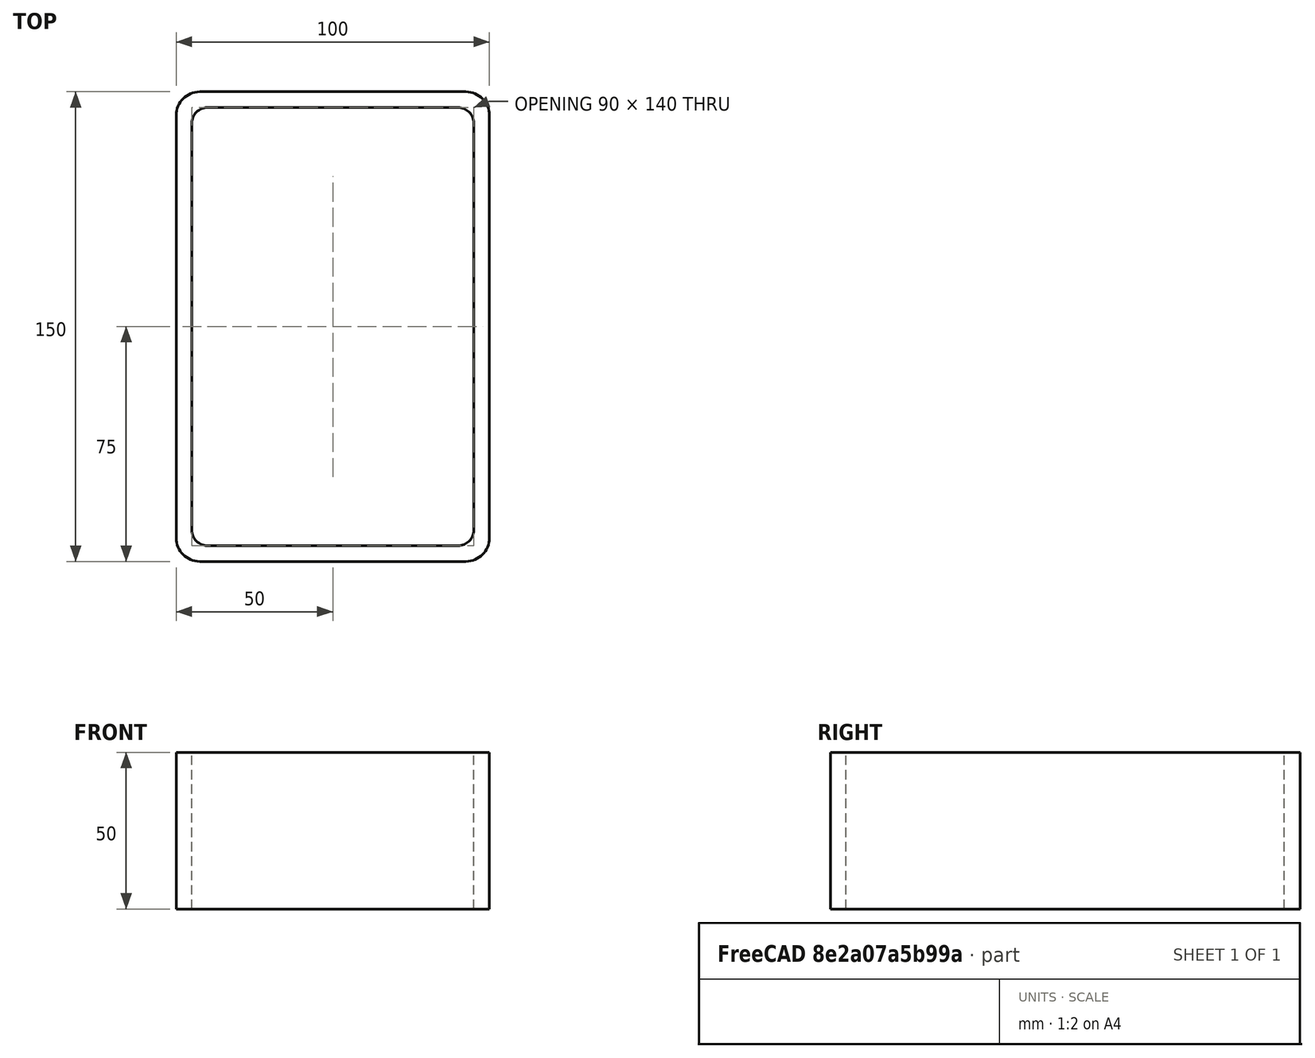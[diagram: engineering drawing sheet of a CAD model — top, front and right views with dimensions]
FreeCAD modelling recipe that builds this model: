
FCSTD DOCUMENT  (FreeCAD 0.15R4671 (Git))
Label: Rectangular hollow section 150x100x5 EN10219 S235JRH
License: All rights reserved
LicenseURL: http://en.wikipedia.org/wiki/All_rights_reserved
objects: Sketcher::SketchObject×1, Part::Extrusion×1
note: 2 computed .brp shape members not serialized (recipe doc carries the construction recipe); baked Part::Feature solids carry a one-line shape summary decoded from their .brp

FEATURE [Sketcher::SketchObject] Sketch
  sketch-geometry (16):
    g0: LineSegment StartX=-40 StartY=70 StartZ=0 EndX=40 EndY=70 EndZ=0
    g1: LineSegment StartX=45 StartY=65 StartZ=0 EndX=45 EndY=-65 EndZ=0
    g2: LineSegment StartX=40 StartY=-70 StartZ=0 EndX=-40 EndY=-70 EndZ=0
    g3: LineSegment StartX=-45 StartY=-65 StartZ=0 EndX=-45 EndY=65 EndZ=0
    g4: LineSegment StartX=-42.5 StartY=75 StartZ=0 EndX=42.5 EndY=75 EndZ=0
    g5: LineSegment StartX=50 StartY=67.5 StartZ=0 EndX=50 EndY=-67.5 EndZ=0
    g6: LineSegment StartX=42.5 StartY=-75 StartZ=0 EndX=-42.5 EndY=-75 EndZ=0
    g7: LineSegment StartX=-50 StartY=-67.5 StartZ=0 EndX=-50 EndY=67.5 EndZ=0
    g8: ArcOfCircle CenterX=-40 CenterY=65 CenterZ=0 NormalX=0 NormalY=0 NormalZ=1 Radius=5 StartAngle=1.5708 EndAngle=3.14159
    g9: ArcOfCircle CenterX=40 CenterY=65 CenterZ=0 NormalX=0 NormalY=0 NormalZ=1 Radius=5 StartAngle=0 EndAngle=1.5708
    g10: ArcOfCircle CenterX=40 CenterY=-65 CenterZ=0 NormalX=0 NormalY=0 NormalZ=1 Radius=5 StartAngle=4.71239 EndAngle=6.28319
    g11: ArcOfCircle CenterX=-40 CenterY=-65 CenterZ=0 NormalX=0 NormalY=0 NormalZ=1 Radius=5 StartAngle=3.14159 EndAngle=4.71239
    g12: ArcOfCircle CenterX=42.5 CenterY=67.5 CenterZ=0 NormalX=0 NormalY=0 NormalZ=1 Radius=7.5 StartAngle=0 EndAngle=1.5708
    g13: ArcOfCircle CenterX=42.5 CenterY=-67.5 CenterZ=0 NormalX=0 NormalY=0 NormalZ=1 Radius=7.5 StartAngle=4.71239 EndAngle=6.28319
    g14: ArcOfCircle CenterX=-42.5 CenterY=-67.5 CenterZ=0 NormalX=0 NormalY=0 NormalZ=1 Radius=7.5 StartAngle=3.14159 EndAngle=4.71239
    g15: ArcOfCircle CenterX=-42.5 CenterY=67.5 CenterZ=0 NormalX=0 NormalY=0 NormalZ=1 Radius=7.5 StartAngle=1.5708 EndAngle=3.14159
  constraints (36):
    c: Horizontal(g2)
    c: Vertical(g3)
    c: Horizontal(g6)
    c: Vertical(g7)
    c: Tangent(g3,g8) = 1.5708
    c: Tangent(g0,g8) = 1.5708
    c: Tangent(g0,g9) = 1.5708
    c: Tangent(g1,g9) = 1.5708
    c: Tangent(g1,g10) = 1.5708
    c: Tangent(g2,g10) = 1.5708
    c: Tangent(g2,g11) = 1.5708
    c: Tangent(g3,g11) = 1.5708
    c: Tangent(g4,g12) = 1.5708
    c: Tangent(g5,g12) = 1.5708
    c: Tangent(g5,g13) = 1.5708
    c: Tangent(g6,g13) = 1.5708
    c: Tangent(g6,g14) = 1.5708
    c: Tangent(g7,g14) = 1.5708
    c: Tangent(g7,g15) = 1.5708
    c: Tangent(g4,g15) = 1.5708
    c: Equal(g9,g8)
    c: Equal(g9,g11)
    c: Equal(g9,g10)
    c: Equal(g12,g15)
    c: Equal(g12,g14)
    c: Equal(g12,g13)
    c: Symmetric(g4,g6,g-1)
    c: Symmetric(g7,g5,g-2)
    c: DistanceY(g4,g6) = -150
    c: DistanceX(g7,g5) = 100
    c: Symmetric(g3,g1,g-2)
    c: Symmetric(g0,g2,g-1)
    c: DistanceY(g0,g4) = 5
    c: DistanceX(g5,g1) = -5
    c: Radius(g9) = 5
    c: Radius(g12) = 7.5
FEATURE [Part::Extrusion] Extrude  label="Rectangular hollow section 150x100x5 EN10219 S235JRH"
  Base = -> Sketch
  Dir = (0,0,50)
  Solid = true
